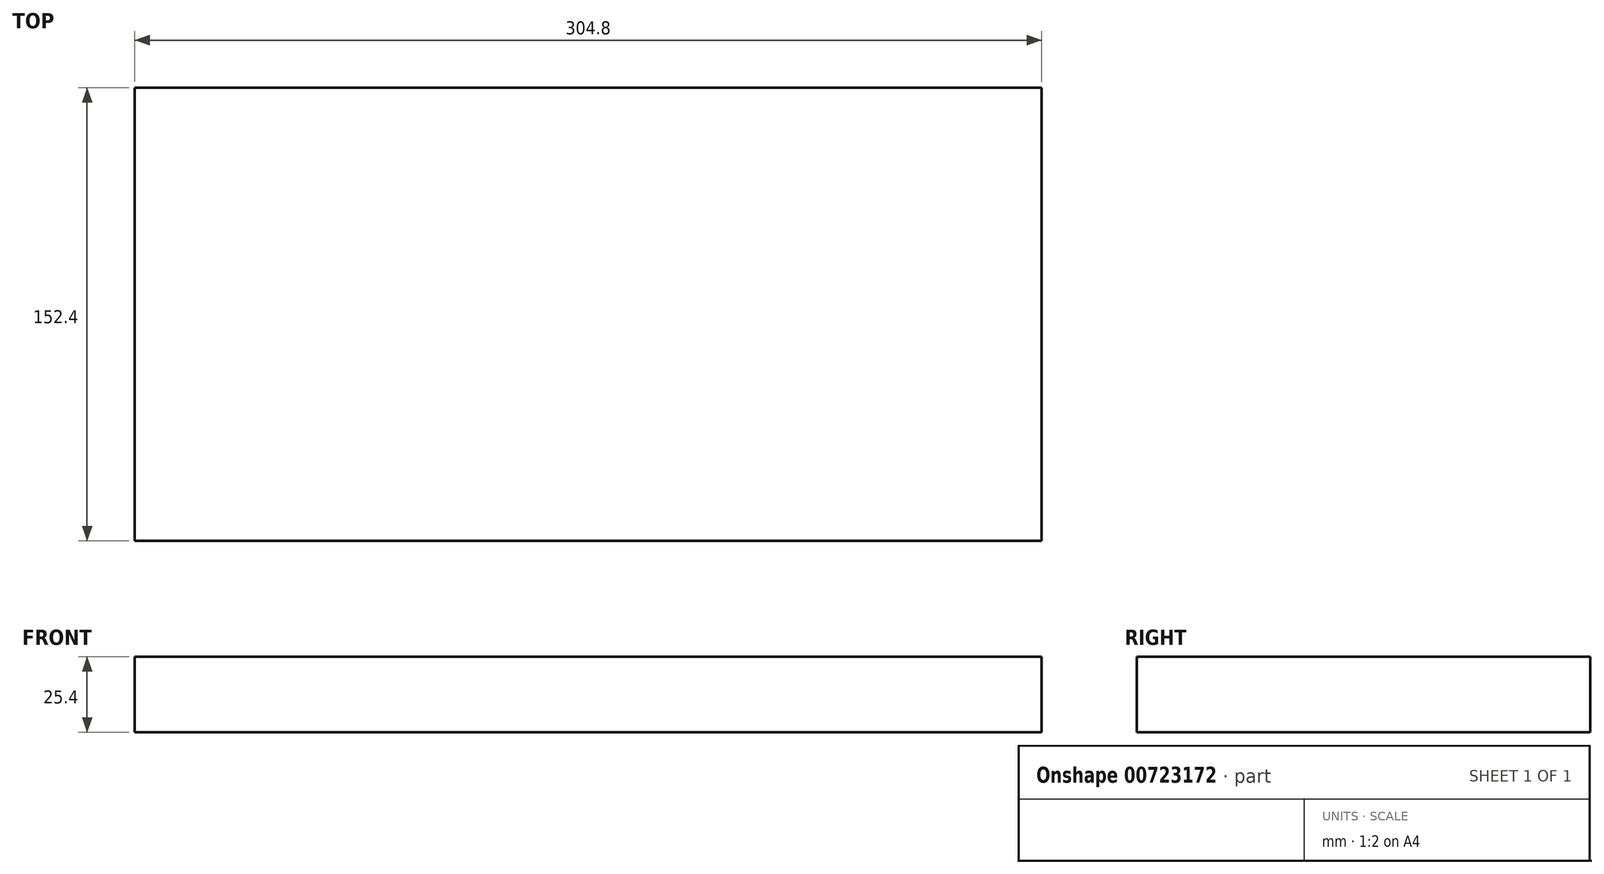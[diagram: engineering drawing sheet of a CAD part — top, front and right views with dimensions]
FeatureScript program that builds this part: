
annotation { "Feature Type Name" : "Feature", "Feature Type Description" : "" }
export const myFeature = defineFeature(function(context is Context, id is Id, definition is map)
    precondition{}
    {
        {
            var Q0;
            Q0=qCreatedBy(makeId("Top.planeOp"),FACE);
            var sketch = newSketch(context, id + "F0", { "sketchPlane" : qUnion([Q0])});
            skLineSegment(sketch, "E0.bottom", {"start": v(152.4, 76.2) * mm, "end": v(-152.4, 76.2) * mm});
            skLineSegment(sketch, "E0.top", {"start": v(152.4, -76.2) * mm, "end": v(-152.4, -76.2) * mm});
            skLineSegment(sketch, "E0.left", {"start": v(152.4, 76.2) * mm, "end": v(152.4, -76.2) * mm});
            skLineSegment(sketch, "E0.right", {"start": v(-152.4, 76.2) * mm, "end": v(-152.4, -76.2) * mm});
            skPoint(sketch, "E0.middle", {"position": v(0, 0) * mm});
            skSolve(sketch);
        }
        {
            var Q0;
            Q0 = qSketchRegion(id + "F0", true);
            extrude(context, id + "F1", {"entities" : qUnion([Q0]), "endBound" : BoundingType.SYMMETRIC, "depth" : 25.4 * mm, "offsetDistance" : 25.4 * mm});
        }
    });
